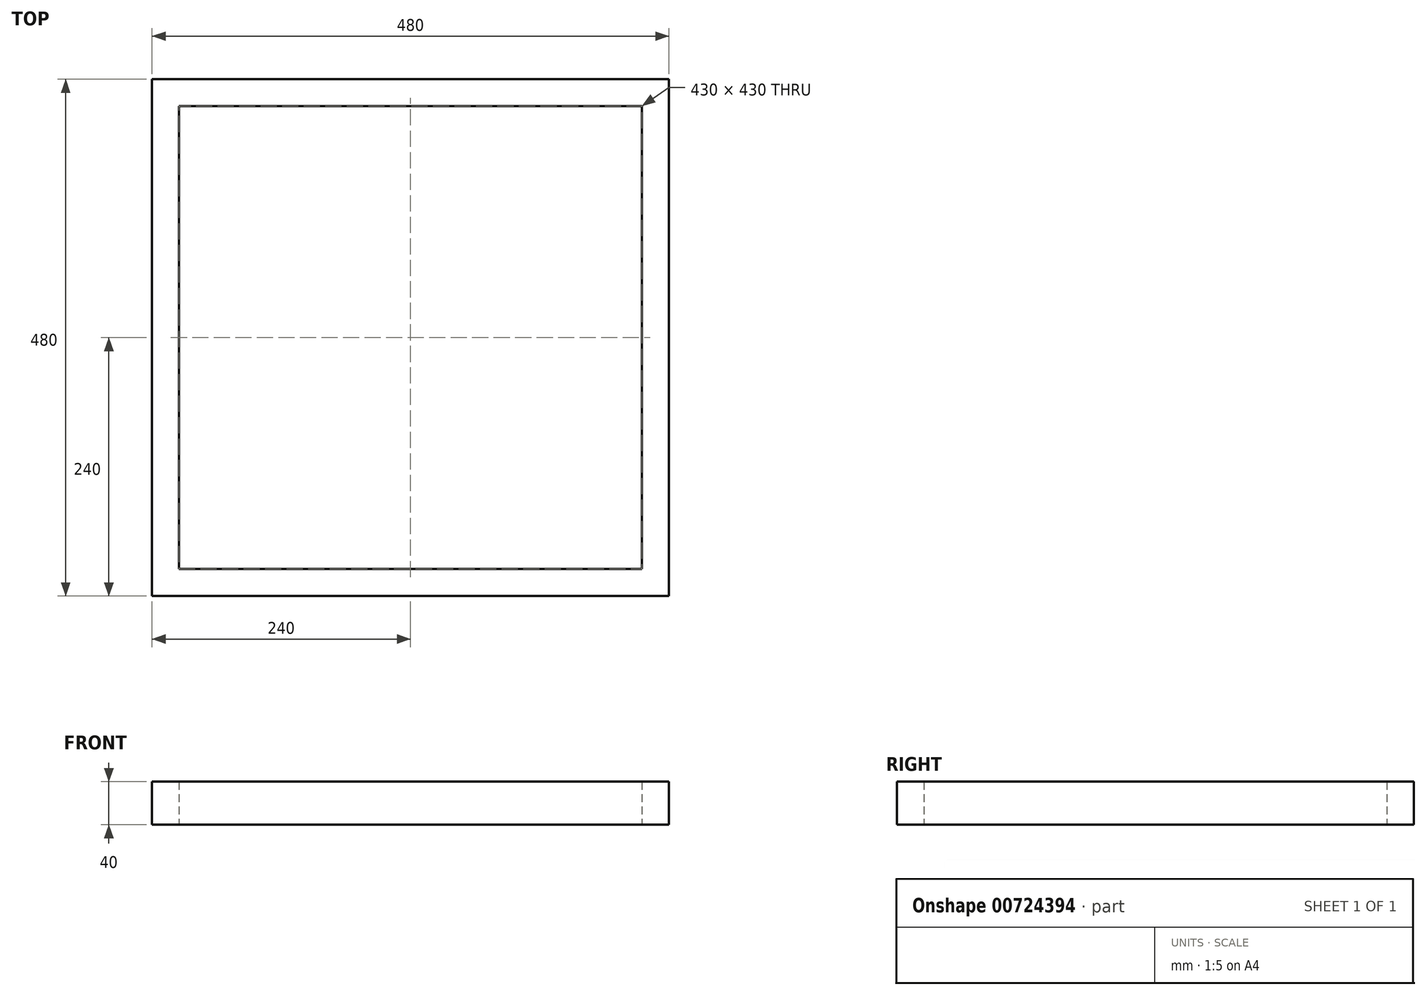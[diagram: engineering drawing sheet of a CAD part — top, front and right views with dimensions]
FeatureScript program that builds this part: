
annotation { "Feature Type Name" : "Feature", "Feature Type Description" : "" }
export const myFeature = defineFeature(function(context is Context, id is Id, definition is map)
    precondition{}
    {
        {
            var Q0;
            Q0=qCreatedBy(makeId("Top.planeOp"),FACE);
            var sketch = newSketch(context, id + "F0", { "sketchPlane" : qUnion([Q0])});
            skLineSegment(sketch, "E0.bottom", {"start": v(0, 0) * mm, "end": v(480, 0) * mm});
            skLineSegment(sketch, "E0.top", {"start": v(0, 480) * mm, "end": v(480, 480) * mm});
            skLineSegment(sketch, "E0.left", {"start": v(0, 0) * mm, "end": v(0, 480) * mm});
            skLineSegment(sketch, "E0.right", {"start": v(480, 0) * mm, "end": v(480, 480) * mm});
            skLineSegment(sketch, "E1.bottom", {"start": v(455, 455) * mm, "end": v(25, 455) * mm});
            skLineSegment(sketch, "E1.top", {"start": v(455, 25) * mm, "end": v(25, 25) * mm});
            skLineSegment(sketch, "E1.left", {"start": v(455, 455) * mm, "end": v(455, 25) * mm});
            skLineSegment(sketch, "E1.right", {"start": v(25, 455) * mm, "end": v(25, 25) * mm});
            skSolve(sketch);
        }
        {
            var Q0;
            Q0=makeQuery(id+"F0.imprint","IMPRINT",FACE,{"disambiguationData":[TD([[makeQuery(id+"F0.imprint","IMPRINT",EDGE,{"derivedFrom":sQuery(id+"F0.wireOp",EDGE,"E0.bottom")}),1.0]])]});
            extrude(context, id + "F1", {"entities" : qUnion([Q0]), "depth" : 40 * mm, "offsetDistance" : 25 * mm});
        }
    });
